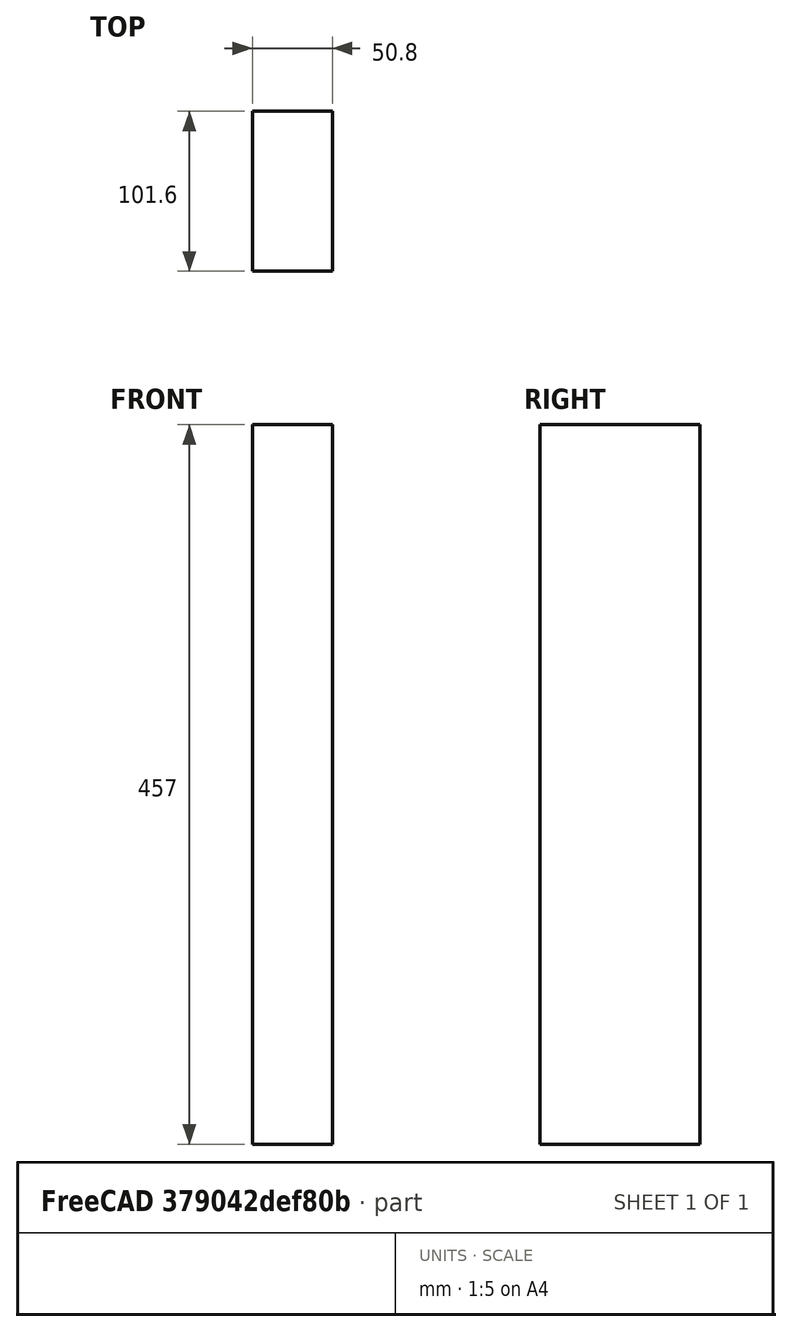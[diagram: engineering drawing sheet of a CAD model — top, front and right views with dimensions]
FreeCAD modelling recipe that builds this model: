
FCSTD DOCUMENT  (FreeCAD 0.19R24276 (Git))
Label: better leg
License: All rights reserved
LicenseURL: http://en.wikipedia.org/wiki/All_rights_reserved
objects: Sketcher::SketchObject×1, PartDesign::Pad×1, PartDesign::Body×1
note: 4 computed .brp shape members not serialized (recipe doc carries the construction recipe); baked Part::Feature solids carry a one-line shape summary decoded from their .brp

FEATURE [Sketcher::SketchObject] Sketch
  FullyConstrained = true
  MapMode = 5
  Support = -> [XY_Plane]
  sketch-geometry (4):
    g0: LineSegment StartX=0 StartY=0 StartZ=0 EndX=50.8 EndY=0 EndZ=0
    g1: LineSegment StartX=50.8 StartY=0 StartZ=0 EndX=50.8 EndY=101.6 EndZ=0
    g2: LineSegment StartX=50.8 StartY=101.6 StartZ=0 EndX=0 EndY=101.6 EndZ=0
    g3: LineSegment StartX=0 StartY=101.6 StartZ=0 EndX=0 EndY=0 EndZ=0
  constraints (11):
    c: Coincident(g0,g1)
    c: Coincident(g1,g2)
    c: Coincident(g2,g3)
    c: Coincident(g3,g0)
    c: Horizontal(g0)
    c: Horizontal(g2)
    c: Vertical(g1)
    c: Vertical(g3)
    c: Coincident(g0,g-1)
    c: DistanceY(g1,g1) = 101.6
    c: DistanceX(g0,g0) = 50.8
FEATURE [PartDesign::Pad] Pad
  Direction = (1,1,1)
  Length = 457
  Length2 = 100
  Profile = -> Sketch
  Type = 0
FEATURE [PartDesign::Body] Body
  Group = -> [Sketch,Pad]
  Origin = -> Origin
  Tip = -> Pad
